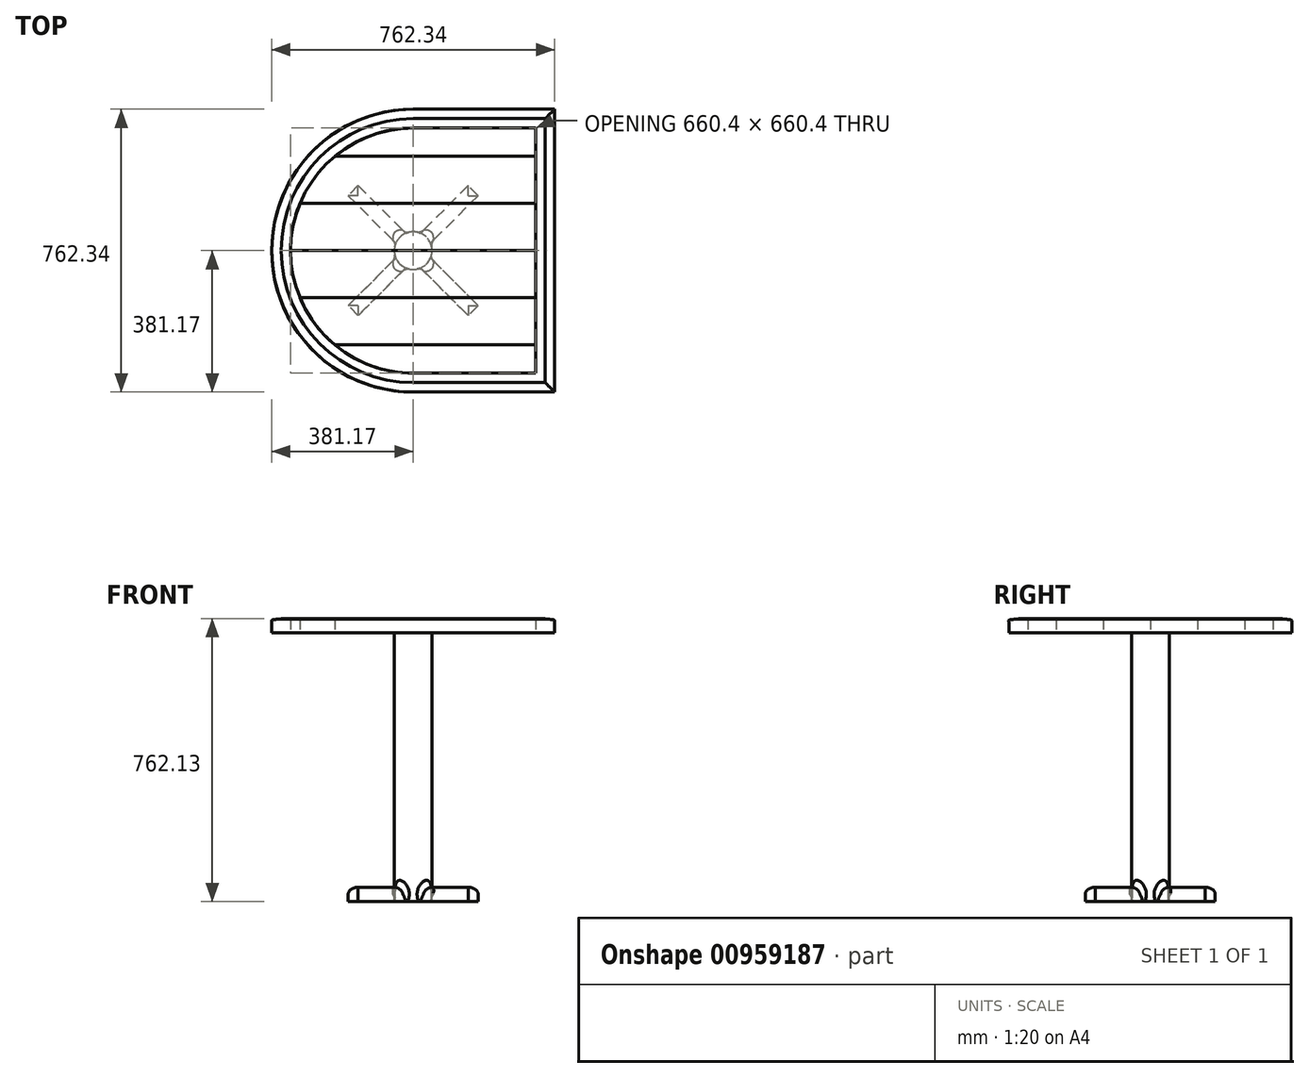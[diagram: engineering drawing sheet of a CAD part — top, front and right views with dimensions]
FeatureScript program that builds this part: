
annotation { "Feature Type Name" : "Feature", "Feature Type Description" : "" }
export const myFeature = defineFeature(function(context is Context, id is Id, definition is map)
    precondition{}
    {
        {
            var Q0;
            Q0=qCreatedBy(makeId("Top.planeOp"),FACE);
            var sketch = newSketch(context, id + "F0", { "sketchPlane" : qUnion([Q0])});
            skLineSegment(sketch, "E0.0", {"start": v(330.2, 330.2) * mm, "end": v(330.2, -330.2) * mm});
            skLineSegment(sketch, "E0.1", {"start": v(0, 330.2) * mm, "end": v(330.2, 330.2) * mm});
            skLineSegment(sketch, "E0.2", {"start": v(0, -330.2) * mm, "end": v(330.2, -330.2) * mm});
            skArc(sketch, "E0.3", {"start": v(-330.2, 0) * mm, "mid": v(-233.49, -233.49) * mm, "end": v(0, -330.2) * mm});
            skArc(sketch, "E0.4", {"start": v(0, 330.2) * mm, "mid": v(-233.49, 233.49) * mm, "end": v(-330.2, 0) * mm});
            skLineSegment(sketch, "E1", {"start": v(0, 330.2) * mm, "end": v(0, 254) * mm, "construction": true});
            skLineSegment(sketch, "E2", {"start": v(330.2, 254) * mm, "end": v(-210.99, 254) * mm});
            skLineSegment(sketch, "E3", {"start": v(0, 254) * mm, "end": v(0, 127) * mm, "construction": true});
            skLineSegment(sketch, "E4", {"start": v(0, 127) * mm, "end": v(0, 0) * mm, "construction": true});
            skLineSegment(sketch, "E5", {"start": v(0, 0) * mm, "end": v(0, -127) * mm, "construction": true});
            skLineSegment(sketch, "E6", {"start": v(0, -127) * mm, "end": v(0, -254) * mm, "construction": true});
            skLineSegment(sketch, "E7", {"start": v(330.2, 127) * mm, "end": v(-304.8, 127) * mm});
            skLineSegment(sketch, "E8", {"start": v(330.2, 0) * mm, "end": v(-330.2, 0) * mm});
            skLineSegment(sketch, "E9", {"start": v(330.2, -127) * mm, "end": v(-304.8, -127) * mm});
            skLineSegment(sketch, "E10", {"start": v(330.2, -254) * mm, "end": v(-210.99, -254) * mm});
            skSolve(sketch);
        }
        {
            var Q0;
            {var subQ0=sQuery(id+"F0.wireOp",EDGE,"E0.1");Q0=makeQuery(id+"F0.imprint","IMPRINT",FACE,{"disambiguationData":[TD([[makeQuery(id+"F0.imprint","IMPRINT",EDGE,{"derivedFrom":subQ0}),-1.0]])]});}
            var Q1;
            {var subQ0=sQuery(id+"F0.wireOp",EDGE,"E7");Q1=makeQuery(id+"F0.imprint","IMPRINT",FACE,{"disambiguationData":[TD([[makeQuery(id+"F0.imprint","IMPRINT",EDGE,{"derivedFrom":subQ0}),1.0]])]});}
            var Q2;
            {var subQ0=sQuery(id+"F0.wireOp",EDGE,"E9");Q2=makeQuery(id+"F0.imprint","IMPRINT",FACE,{"disambiguationData":[TD([[makeQuery(id+"F0.imprint","IMPRINT",EDGE,{"derivedFrom":subQ0}),1.0]])]});}
            extrude(context, id + "F1", {"entities" : qUnion([Q0, Q1, Q2]), "depth" : 38.23 * mm, "offsetDistance" : 25.4 * mm});
        }
        {
            var Q0;
            {var subQ0=sQuery(id+"F0.wireOp",EDGE,"E2");Q0=makeQuery(id+"F0.imprint","IMPRINT",FACE,{"disambiguationData":[TD([[makeQuery(id+"F0.imprint","IMPRINT",EDGE,{"derivedFrom":subQ0}),1.0]])]});}
            var Q1;
            {var subQ0=sQuery(id+"F0.wireOp",EDGE,"E8");Q1=makeQuery(id+"F0.imprint","IMPRINT",FACE,{"disambiguationData":[TD([[makeQuery(id+"F0.imprint","IMPRINT",EDGE,{"derivedFrom":subQ0}),1.0]])]});}
            var Q2;
            {var subQ0=sQuery(id+"F0.wireOp",EDGE,"E0.2");Q2=makeQuery(id+"F0.imprint","IMPRINT",FACE,{"disambiguationData":[TD([[makeQuery(id+"F0.imprint","IMPRINT",EDGE,{"derivedFrom":subQ0}),1.0]])]});}
            extrude(context, id + "F2", {"entities" : qUnion([Q0, Q1, Q2]), "depth" : 38.1 * mm, "offsetDistance" : 25.4 * mm});
        }
        {
            var Q0;
            Q0=qCreatedBy(makeId("Right.planeOp"),FACE);
            var sketch = newSketch(context, id + "F3", { "sketchPlane" : qUnion([Q0])});
            skLineSegment(sketch, "E11", {"start": v(-328.8, 0.13) * mm, "end": v(-381, 0.13) * mm});
            skLineSegment(sketch, "E12", {"start": v(-469.86, 366.54) * mm, "end": v(-469.86, 366.54) * mm});
            skLineSegment(sketch, "E13", {"start": v(-463.51, 372.89) * mm, "end": v(-463.51, 372.89) * mm});
            skLineSegment(sketch, "E14", {"start": v(-355.6, 38.23) * mm, "end": v(-330.2, 38.23) * mm});
            skPoint(sketch, "E15.visualSharp", {"position": v(-395.35, 38.23) * mm});
            skPoint(sketch, "E16.visualSharp", {"position": v(-395.35, 6.35) * mm});
            skLineSegment(sketch, "E17", {"start": v(-330.2, 38.23) * mm, "end": v(-330.2, 0) * mm});
            skLineSegment(sketch, "E18", {"start": v(-355.6, 38.23) * mm, "end": v(-355.6, 36.64) * mm});
            skLineSegment(sketch, "E19", {"start": v(-381, 0.13) * mm, "end": v(-381, 28.7) * mm});
            skFitSpline(sketch, "E20", {"points": [v(-355.6, 36.64) * mm, v(-379.9, 34.36) * mm, v(-381, 28.7) * mm], "startDerivative": vector(-20.98, 0) * mm, "endDerivative": vector(0, -34.65) * mm});
            skLineSegment(sketch, "E21", {"start": v(-357.26, 36.64) * mm, "end": v(-355.6, 36.64) * mm, "construction": true});
            skSolve(sketch);
        }
        {
            var Q0;
            {var subQ1=sQuery(id+"F3.wireOp",EDGE,"E14");Q0=makeQuery(id+"F3.imprint","IMPRINT",FACE,{"disambiguationData":[TD([[makeQuery(id+"F3.imprint","IMPRINT",EDGE,{"derivedFrom":subQ1}),-1.0]])]});}
            var Q1;
            Q1=sQuery(id+"F0.wireOp",EDGE,"E0.2");
            var Q2;
            Q2=sQuery(id+"F0.wireOp",EDGE,"E0.3");
            var Q3;
            Q3=sQuery(id+"F0.wireOp",EDGE,"E0.0");
            var Q4;
            Q4=sQuery(id+"F0.wireOp",EDGE,"E0.1");
            var Q5;
            Q5=sQuery(id+"F0.wireOp",EDGE,"E0.4");
            sweep(context, id + "F4", {"profiles" : qUnion([Q0]), "path" : qUnion([Q1, Q2, Q3, Q4, Q5])});
        }
        {
            var Q0;
            Q0=qCreatedBy(makeId("Top.planeOp"),FACE);
            var sketch = newSketch(context, id + "F5", { "sketchPlane" : qUnion([Q0])});
            skCircle(sketch, "E22", {"center": v(0, 0) * mm, "radius": 50.8 * mm});
            skSolve(sketch);
        }
        {
            var Q0;
            Q0 = qSketchRegion(id + "F5", true);
            extrude(context, id + "F6", {"entities" : qUnion([Q0]), "oppositeDirection" : true, "depth" : 723.9 * mm, "offsetDistance" : 25.4 * mm});
        }
        {
            var Q0;
            Q0=makeQuery(id+"F6.opExtrude","CAP_FACE",FACE,{"disambiguationData":[OSD([sQuery(id+"F5.wireOp",EDGE,"E22")])],"isStart":false});
            var sketch = newSketch(context, id + "F7", { "sketchPlane" : qUnion([Q0])});
            skLineSegment(sketch, "E23.bottom", {"start": v(175.11, -148.17) * mm, "end": v(26.94, 0) * mm});
            skLineSegment(sketch, "E23.top", {"start": v(148.17, -175.11) * mm, "end": v(0, -26.94) * mm});
            skLineSegment(sketch, "E23.left", {"start": v(175.11, -148.17) * mm, "end": v(148.17, -175.11) * mm});
            skLineSegment(sketch, "E23.right", {"start": v(-148.17, 175.11) * mm, "end": v(-175.11, 148.17) * mm});
            skPoint(sketch, "E23.middle", {"position": v(0, 0) * mm});
            skLineSegment(sketch, "E24.1.0", {"start": v(-148.17, -175.11) * mm, "end": v(-175.11, -148.17) * mm});
            skLineSegment(sketch, "E24.1.1", {"start": v(-148.17, -175.11) * mm, "end": v(0, -26.94) * mm});
            skLineSegment(sketch, "E24.1.2", {"start": v(175.11, 148.17) * mm, "end": v(148.17, 175.11) * mm});
            skLineSegment(sketch, "E24.1.3", {"start": v(-175.11, -148.17) * mm, "end": v(-26.94, 0) * mm});
            skLineSegment(sketch, "E24.anchor1", {"start": v(0, 0) * mm, "end": v(148.17, -175.11) * mm, "construction": true});
            skLineSegment(sketch, "E24.anchor2", {"start": v(0, 0) * mm, "end": v(-175.11, -148.17) * mm, "construction": true});
            skLineSegment(sketch, "E25.trimOffspring", {"start": v(0, 26.94) * mm, "end": v(-148.17, 175.11) * mm});
            skLineSegment(sketch, "E26.trimOffspring", {"start": v(0, 26.94) * mm, "end": v(148.17, 175.11) * mm});
            skLineSegment(sketch, "E27.trimOffspring", {"start": v(26.94, 0) * mm, "end": v(175.11, 148.17) * mm});
            skLineSegment(sketch, "E28.trimOffspring", {"start": v(-26.94, 0) * mm, "end": v(-175.11, 148.17) * mm});
            skSolve(sketch);
        }
        {
            var Q0;
            Q0 = qSketchRegion(id + "F7", true);
            extrude(context, id + "F8", {"entities" : qUnion([Q0]), "operationType" : NewBodyOperationType.ADD, "oppositeDirection" : true, "depth" : 38.1 * mm, "offsetDistance" : 25.4 * mm});
        }
        {
            var Q0;
            {var subQ0=sQuery(id+"F7.wireOp",EDGE,"E23.right");var subQ1=sQuery(id+"F7.wireOp",EDGE,"E25.trimOffspring");var subQ2=sQuery(id+"F7.wireOp",EDGE,"E28.trimOffspring");Q0=makeQuery(id+"F8.boolean.opBoolean","SPLIT",FACE,{"disambiguationData":[TD([makeQuery(id+"F8.opExtrude","SWEPT_FACE",FACE,{"disambiguationData":[OSD([subQ0])]})])],"derivedFrom":makeQuery(id+"F8.opExtrude","CAP_FACE",FACE,{"disambiguationData":[OSD([sQuery(id+"F7.wireOp",EDGE,"E23.bottom"),sQuery(id+"F7.wireOp",EDGE,"E23.top"),sQuery(id+"F7.wireOp",EDGE,"E23.left"),subQ0,sQuery(id+"F7.wireOp",EDGE,"E24.1.0"),sQuery(id+"F7.wireOp",EDGE,"E24.1.1"),sQuery(id+"F7.wireOp",EDGE,"E24.1.2"),sQuery(id+"F7.wireOp",EDGE,"E24.1.3"),subQ1,sQuery(id+"F7.wireOp",EDGE,"E26.trimOffspring"),sQuery(id+"F7.wireOp",EDGE,"E27.trimOffspring"),subQ2])],"isStart":false})});}
            var Q1;
            {var subQ0=sQuery(id+"F7.wireOp",EDGE,"E24.1.1");var subQ1=sQuery(id+"F7.wireOp",EDGE,"E24.1.0");var subQ2=sQuery(id+"F7.wireOp",EDGE,"E24.1.3");Q1=makeQuery(id+"F8.boolean.opBoolean","SPLIT",FACE,{"disambiguationData":[TD([makeQuery(id+"F8.opExtrude","SWEPT_FACE",FACE,{"disambiguationData":[OSD([subQ1])]})])],"derivedFrom":makeQuery(id+"F8.opExtrude","CAP_FACE",FACE,{"disambiguationData":[OSD([sQuery(id+"F7.wireOp",EDGE,"E23.bottom"),sQuery(id+"F7.wireOp",EDGE,"E23.top"),sQuery(id+"F7.wireOp",EDGE,"E23.left"),sQuery(id+"F7.wireOp",EDGE,"E23.right"),subQ1,subQ0,sQuery(id+"F7.wireOp",EDGE,"E24.1.2"),subQ2,sQuery(id+"F7.wireOp",EDGE,"E25.trimOffspring"),sQuery(id+"F7.wireOp",EDGE,"E26.trimOffspring"),sQuery(id+"F7.wireOp",EDGE,"E27.trimOffspring"),sQuery(id+"F7.wireOp",EDGE,"E28.trimOffspring")])],"isStart":false})});}
            var Q2;
            {var subQ0=sQuery(id+"F7.wireOp",EDGE,"E23.bottom");var subQ1=sQuery(id+"F7.wireOp",EDGE,"E23.top");var subQ2=sQuery(id+"F7.wireOp",EDGE,"E23.left");Q2=makeQuery(id+"F8.boolean.opBoolean","SPLIT",FACE,{"disambiguationData":[TD([makeQuery(id+"F8.opExtrude","SWEPT_FACE",FACE,{"disambiguationData":[OSD([subQ0])]})])],"derivedFrom":makeQuery(id+"F8.opExtrude","CAP_FACE",FACE,{"disambiguationData":[OSD([subQ0,subQ1,subQ2,sQuery(id+"F7.wireOp",EDGE,"E23.right"),sQuery(id+"F7.wireOp",EDGE,"E24.1.0"),sQuery(id+"F7.wireOp",EDGE,"E24.1.1"),sQuery(id+"F7.wireOp",EDGE,"E24.1.2"),sQuery(id+"F7.wireOp",EDGE,"E24.1.3"),sQuery(id+"F7.wireOp",EDGE,"E25.trimOffspring"),sQuery(id+"F7.wireOp",EDGE,"E26.trimOffspring"),sQuery(id+"F7.wireOp",EDGE,"E27.trimOffspring"),sQuery(id+"F7.wireOp",EDGE,"E28.trimOffspring")])],"isStart":false})});}
            var Q3;
            {var subQ0=sQuery(id+"F7.wireOp",EDGE,"E27.trimOffspring");var subQ1=sQuery(id+"F7.wireOp",EDGE,"E24.1.2");var subQ2=sQuery(id+"F7.wireOp",EDGE,"E26.trimOffspring");Q3=makeQuery(id+"F8.boolean.opBoolean","SPLIT",FACE,{"disambiguationData":[TD([makeQuery(id+"F8.opExtrude","SWEPT_FACE",FACE,{"disambiguationData":[OSD([subQ1])]})])],"derivedFrom":makeQuery(id+"F8.opExtrude","CAP_FACE",FACE,{"disambiguationData":[OSD([sQuery(id+"F7.wireOp",EDGE,"E23.bottom"),sQuery(id+"F7.wireOp",EDGE,"E23.top"),sQuery(id+"F7.wireOp",EDGE,"E23.left"),sQuery(id+"F7.wireOp",EDGE,"E23.right"),sQuery(id+"F7.wireOp",EDGE,"E24.1.0"),sQuery(id+"F7.wireOp",EDGE,"E24.1.1"),subQ1,sQuery(id+"F7.wireOp",EDGE,"E24.1.3"),sQuery(id+"F7.wireOp",EDGE,"E25.trimOffspring"),subQ2,subQ0,sQuery(id+"F7.wireOp",EDGE,"E28.trimOffspring")])],"isStart":false})});}
            fillet(context, id + "F9", {"entities" : qUnion([Q0, Q1, Q2, Q3]), "radius" : 19.05 * mm, "tangentPropagation" : true, "allowEdgeOverflow" : false});
        }
    });
